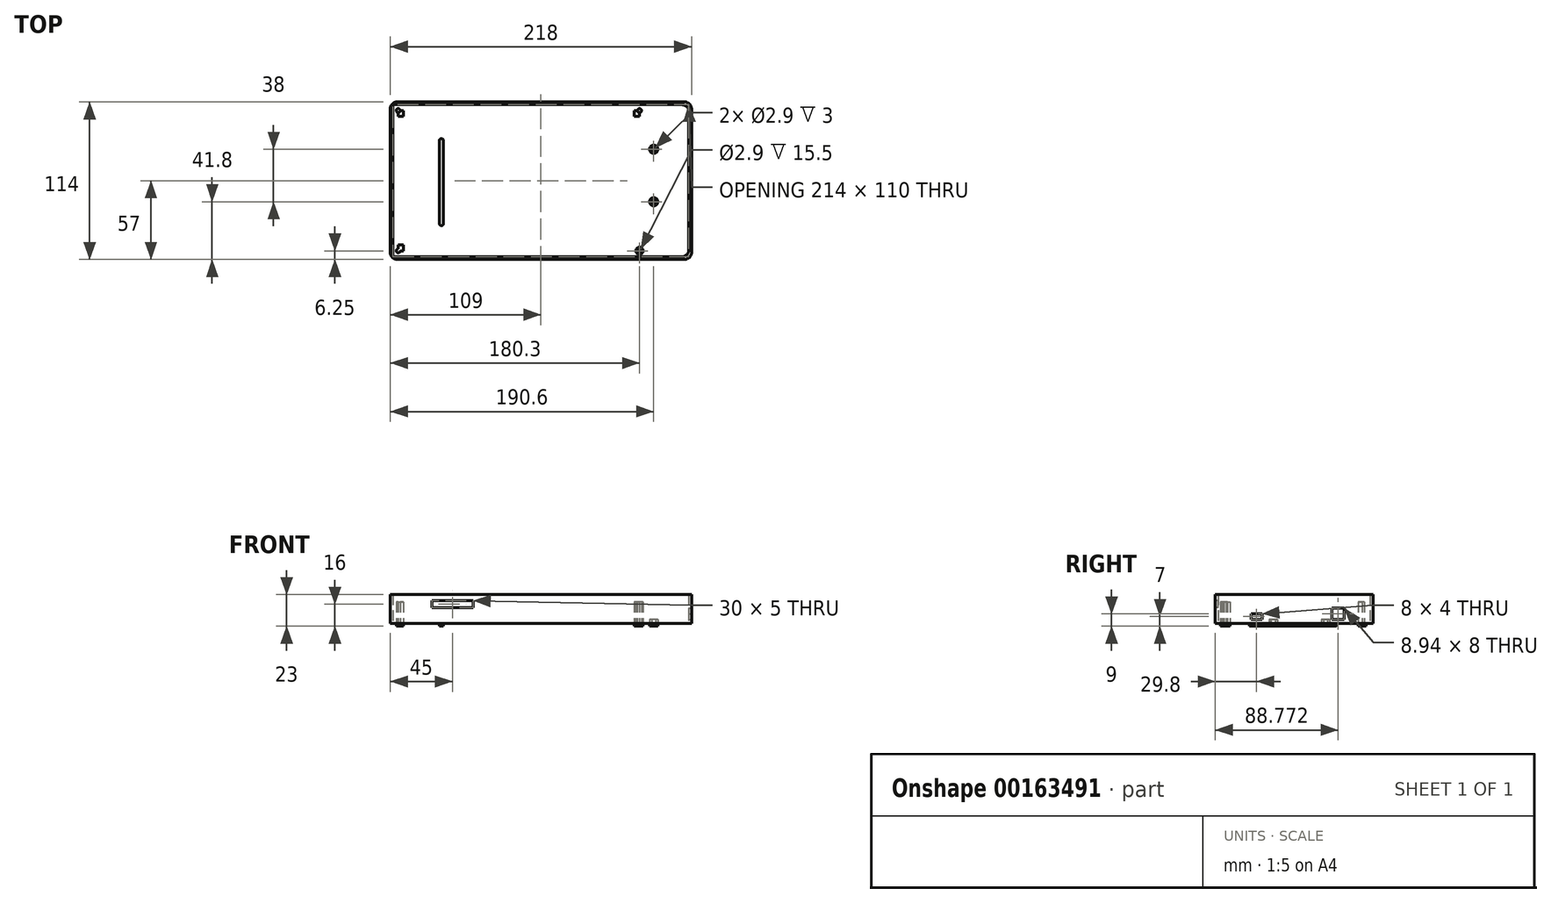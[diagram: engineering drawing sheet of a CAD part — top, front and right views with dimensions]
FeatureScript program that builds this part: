
annotation { "Feature Type Name" : "Feature", "Feature Type Description" : "" }
export const myFeature = defineFeature(function(context is Context, id is Id, definition is map)
    precondition{}
    {
        {
            var Q0;
            Q0=qCreatedBy(makeId("Top.planeOp"),FACE);
            var sketch = newSketch(context, id + "F0", { "sketchPlane" : qUnion([Q0])});
            skLineSegment(sketch, "E0.bottom", {"start": v(87.3, -50.75) * mm, "end": v(-87.3, -50.75) * mm});
            skLineSegment(sketch, "E0.top", {"start": v(87.3, 50.75) * mm, "end": v(-87.3, 50.75) * mm});
            skLineSegment(sketch, "E0.left", {"start": v(87.3, -50.75) * mm, "end": v(87.3, 50.75) * mm});
            skLineSegment(sketch, "E0.right", {"start": v(-87.3, -50.75) * mm, "end": v(-87.3, 50.75) * mm});
            skPoint(sketch, "E0.middle", {"position": v(0, 0) * mm});
            skLineSegment(sketch, "E1.bottom", {"start": v(87.3, 38.3) * mm, "end": v(121, 38.3) * mm, "construction": true});
            skLineSegment(sketch, "E1.top", {"start": v(87.3, -31.2) * mm, "end": v(121, -31.2) * mm, "construction": true});
            skLineSegment(sketch, "E1.left", {"start": v(87.3, 38.3) * mm, "end": v(87.3, -31.2) * mm, "construction": true});
            skLineSegment(sketch, "E1.right", {"start": v(121, 38.3) * mm, "end": v(121, -31.2) * mm, "construction": true});
            skLineSegment(sketch, "E2.bottom", {"start": v(91, -55) * mm, "end": v(-91, -55) * mm});
            skLineSegment(sketch, "E2.top", {"start": v(91, 55) * mm, "end": v(-91, 55) * mm});
            skLineSegment(sketch, "E2.left", {"start": v(91, -55) * mm, "end": v(91, 55) * mm, "construction": true});
            skLineSegment(sketch, "E2.right", {"start": v(-91, -55) * mm, "end": v(-91, 55) * mm});
            skLineSegment(sketch, "E3.bottom", {"start": v(101.5, 38.3) * mm, "end": v(121, 38.3) * mm, "construction": true});
            skLineSegment(sketch, "E3.top", {"start": v(101.5, 27.3) * mm, "end": v(121, 27.3) * mm, "construction": true});
            skLineSegment(sketch, "E3.left", {"start": v(101.5, 38.3) * mm, "end": v(101.5, 27.3) * mm, "construction": true});
            skLineSegment(sketch, "E3.right", {"start": v(121, 38.3) * mm, "end": v(121, 27.3) * mm, "construction": true});
            skLineSegment(sketch, "E4.bottom", {"start": v(-63, -55) * mm, "end": v(-33, -55) * mm, "construction": true});
            skLineSegment(sketch, "E4.top", {"start": v(-63, -33) * mm, "end": v(-33, -33) * mm, "construction": true});
            skLineSegment(sketch, "E4.left", {"start": v(-63, -55) * mm, "end": v(-63, -33) * mm, "construction": true});
            skLineSegment(sketch, "E4.right", {"start": v(-33, -55) * mm, "end": v(-33, -33) * mm, "construction": true});
            skLineSegment(sketch, "E5.bottom", {"start": v(121, 22.8) * mm, "end": v(97.6, 22.8) * mm, "construction": true});
            skLineSegment(sketch, "E5.top", {"start": v(121, -15.2) * mm, "end": v(97.6, -15.2) * mm, "construction": true});
            skLineSegment(sketch, "E5.left", {"start": v(121, 22.8) * mm, "end": v(121, -15.2) * mm, "construction": true});
            skLineSegment(sketch, "E5.right", {"start": v(97.6, 22.8) * mm, "end": v(97.6, -15.2) * mm, "construction": true});
            skLineSegment(sketch, "E6.top", {"start": v(121, -8.2) * mm, "end": v(117, -8.2) * mm, "construction": true});
            skLineSegment(sketch, "E6.left", {"start": v(121, -31.2) * mm, "end": v(121, -8.2) * mm, "construction": true});
            skLineSegment(sketch, "E6.right", {"start": v(117, -31.2) * mm, "end": v(117, -8.2) * mm, "construction": true});
            skLineSegment(sketch, "E7.bottom", {"start": v(121, -31.2) * mm, "end": v(101, -31.2) * mm, "construction": true});
            skLineSegment(sketch, "E7.top", {"start": v(121, -27.2) * mm, "end": v(101, -27.2) * mm, "construction": true});
            skLineSegment(sketch, "E7.left", {"start": v(121, -31.2) * mm, "end": v(121, -27.2) * mm, "construction": true});
            skLineSegment(sketch, "E7.right", {"start": v(101, -31.2) * mm, "end": v(101, -27.2) * mm, "construction": true});
            skLineSegment(sketch, "E8.bottom", {"start": v(-93, 57) * mm, "end": v(125, 57) * mm});
            skLineSegment(sketch, "E8.top", {"start": v(-93, -57) * mm, "end": v(125, -57) * mm});
            skLineSegment(sketch, "E8.left", {"start": v(-93, 57) * mm, "end": v(-93, -57) * mm});
            skLineSegment(sketch, "E8.right", {"start": v(125, 57) * mm, "end": v(125, -57) * mm});
            skCircle(sketch, "E9", {"center": v(-87.3, 50.75) * mm, "radius": 1.45 * mm});
            skCircle(sketch, "E10", {"center": v(-87.3, -50.75) * mm, "radius": 1.45 * mm});
            skCircle(sketch, "E11", {"center": v(87.3, 50.75) * mm, "radius": 1.45 * mm});
            skCircle(sketch, "E12", {"center": v(97.6, 22.8) * mm, "radius": 1.45 * mm});
            skCircle(sketch, "E13", {"center": v(97.6, -15.2) * mm, "radius": 1.45 * mm});
            skCircle(sketch, "E14", {"center": v(117, -8.2) * mm, "radius": 1.75 * mm});
            skCircle(sketch, "E15", {"center": v(101, -27.2) * mm, "radius": 1.75 * mm});
            skCircle(sketch, "E16", {"center": v(97.6, 22.8) * mm, "radius": 3 * mm});
            skCircle(sketch, "E17", {"center": v(97.6, -15.2) * mm, "radius": 3 * mm});
            skLineSegment(sketch, "E18", {"start": v(91, 55) * mm, "end": v(123, 55) * mm});
            skLineSegment(sketch, "E19", {"start": v(123, 55) * mm, "end": v(123, -55) * mm});
            skLineSegment(sketch, "E20", {"start": v(123, -55) * mm, "end": v(91, -55) * mm});
            skLineSegment(sketch, "E21.bottom", {"start": v(-91, 55) * mm, "end": v(-83.6, 55) * mm});
            skLineSegment(sketch, "E21.top", {"start": v(-91, 46.5) * mm, "end": v(-83.6, 46.5) * mm});
            skLineSegment(sketch, "E21.left", {"start": v(-91, 55) * mm, "end": v(-91, 46.5) * mm});
            skLineSegment(sketch, "E21.right", {"start": v(-83.6, 55) * mm, "end": v(-83.6, 46.5) * mm});
            skLineSegment(sketch, "E22.bottom", {"start": v(91, 55) * mm, "end": v(83.6, 55) * mm});
            skLineSegment(sketch, "E22.top", {"start": v(91, 46.5) * mm, "end": v(83.6, 46.5) * mm});
            skLineSegment(sketch, "E22.left", {"start": v(91, 55) * mm, "end": v(91, 46.5) * mm});
            skLineSegment(sketch, "E22.right", {"start": v(83.6, 55) * mm, "end": v(83.6, 46.5) * mm});
            skLineSegment(sketch, "E23.bottom", {"start": v(-91, -55) * mm, "end": v(-83.6, -55) * mm});
            skLineSegment(sketch, "E23.top", {"start": v(-91, -46.5) * mm, "end": v(-83.6, -46.5) * mm});
            skLineSegment(sketch, "E23.left", {"start": v(-91, -55) * mm, "end": v(-91, -46.5) * mm});
            skLineSegment(sketch, "E23.right", {"start": v(-83.6, -55) * mm, "end": v(-83.6, -46.5) * mm});
            skCircle(sketch, "E24", {"center": v(87.3, -50.75) * mm, "radius": 1.45 * mm});
            skCircle(sketch, "E25", {"center": v(87.3, -50.75) * mm, "radius": 2.62 * mm});
            skLineSegment(sketch, "E26.bottom", {"start": v(84.68, -50.75) * mm, "end": v(89.98, -50.75) * mm});
            skLineSegment(sketch, "E26.top", {"start": v(84.68, -55) * mm, "end": v(89.98, -55) * mm});
            skLineSegment(sketch, "E26.left", {"start": v(84.68, -50.75) * mm, "end": v(84.68, -55) * mm});
            skLineSegment(sketch, "E26.right", {"start": v(89.98, -50.75) * mm, "end": v(89.98, -55) * mm});
            skSolve(sketch);
        }
        {
            var Q0;
            {var subQ1=sQuery(id+"F0.wireOp",EDGE,"E0.bottom");var subQ5=sQuery(id+"F0.wireOp",EDGE,"E23.right");var subQ6=makeQuery(id+"F0.imprint","INTERSECT",VERTEX,{"derivedFrom":[subQ1,subQ5]});Q0=makeQuery(id+"F0.imprint","IMPRINT",FACE,{"disambiguationData":[TD([[makeQuery(id+"F0.imprint","IMPRINT",EDGE,{"disambiguationData":[TD([[subQ6,-1.0]])],"derivedFrom":subQ1}),-1.0]])]});}
            var Q1;
            {var subQ0=sQuery(id+"F0.wireOp",EDGE,"E0.right");var subQ1=sQuery(id+"F0.wireOp",EDGE,"E0.bottom");var subQ2=makeQuery(id+"F0.imprint","INTERSECT",VERTEX,{"derivedFrom":[subQ1,subQ0]});Q1=makeQuery(id+"F0.imprint","IMPRINT",FACE,{"disambiguationData":[TD([[makeQuery(id+"F0.imprint","IMPRINT",EDGE,{"disambiguationData":[TD([[subQ2,1.0]])],"derivedFrom":subQ1}),1.0]])]});}
            var Q2;
            Q2=makeQuery(id+"F0.imprint","IMPRINT",FACE,{"disambiguationData":[TD([[makeQuery(id+"F0.imprint","IMPRINT",EDGE,{"derivedFrom":sQuery(id+"F0.wireOp",EDGE,"E2.top")}),-1.0]])]});
            var Q3;
            {var subQ5=sQuery(id+"F0.wireOp",EDGE,"E2.right");Q3=makeQuery(id+"F0.imprint","IMPRINT",FACE,{"disambiguationData":[TD([[makeQuery(id+"F0.imprint","IMPRINT",EDGE,{"derivedFrom":subQ5}),-1.0]])]});}
            var Q4;
            {var subQ8=sQuery(id+"F0.wireOp",EDGE,"E23.bottom");Q4=makeQuery(id+"F0.imprint","IMPRINT",FACE,{"disambiguationData":[TD([[makeQuery(id+"F0.imprint","IMPRINT",EDGE,{"derivedFrom":subQ8}),1.0]])]});}
            var Q5;
            {var subQ0=sQuery(id+"F0.wireOp",EDGE,"E22.bottom");Q5=makeQuery(id+"F0.imprint","IMPRINT",FACE,{"disambiguationData":[TD([[makeQuery(id+"F0.imprint","IMPRINT",EDGE,{"derivedFrom":subQ0}),1.0]])]});}
            var Q6;
            {var subQ0=sQuery(id+"F0.wireOp",EDGE,"E22.right");var subQ3=sQuery(id+"F0.wireOp",EDGE,"E0.top");var subQ4=makeQuery(id+"F0.imprint","INTERSECT",VERTEX,{"derivedFrom":[subQ3,subQ0]});Q6=makeQuery(id+"F0.imprint","IMPRINT",FACE,{"disambiguationData":[TD([[makeQuery(id+"F0.imprint","IMPRINT",EDGE,{"disambiguationData":[TD([[subQ4,-1.0]])],"derivedFrom":subQ3}),1.0]])]});}
            var Q7;
            Q7=makeQuery(id+"F0.imprint","IMPRINT",FACE,{"disambiguationData":[TD([[makeQuery(id+"F0.imprint","IMPRINT",EDGE,{"derivedFrom":sQuery(id+"F0.wireOp",EDGE,"E13")}),-1.0]])]});
            var Q8;
            {var subQ0=sQuery(id+"F0.wireOp",EDGE,"E26.left");Q8=makeQuery(id+"F0.imprint","IMPRINT",FACE,{"disambiguationData":[TD([[makeQuery(id+"F0.imprint","IMPRINT",EDGE,{"derivedFrom":subQ0}),-1.0]])]});}
            var Q9;
            {var subQ0=sQuery(id+"F0.wireOp",EDGE,"E21.right");var subQ7=sQuery(id+"F0.wireOp",EDGE,"E0.top");var subQ9=makeQuery(id+"F0.imprint","INTERSECT",VERTEX,{"derivedFrom":[subQ7,subQ0]});Q9=makeQuery(id+"F0.imprint","IMPRINT",FACE,{"disambiguationData":[TD([[makeQuery(id+"F0.imprint","IMPRINT",EDGE,{"disambiguationData":[TD([[subQ9,-1.0]])],"derivedFrom":subQ7}),1.0]])]});}
            var Q10;
            {var subQ5=sQuery(id+"F0.wireOp",EDGE,"E2.top");Q10=makeQuery(id+"F0.imprint","IMPRINT",FACE,{"disambiguationData":[TD([[makeQuery(id+"F0.imprint","IMPRINT",EDGE,{"derivedFrom":subQ5}),1.0]])]});}
            var Q11;
            {var subQ0=sQuery(id+"F0.wireOp",EDGE,"E11");var subQ1=sQuery(id+"F0.wireOp",EDGE,"E0.top");var subQ2=makeQuery(id+"F0.imprint","INTERSECT",VERTEX,{"derivedFrom":[subQ1,subQ0]});Q11=makeQuery(id+"F0.imprint","IMPRINT",FACE,{"disambiguationData":[TD([[makeQuery(id+"F0.imprint","IMPRINT",EDGE,{"disambiguationData":[TD([[subQ2,-1.0]])],"derivedFrom":subQ1}),1.0]])]});}
            var Q12;
            Q12=makeQuery(id+"F0.imprint","IMPRINT",FACE,{"disambiguationData":[TD([[makeQuery(id+"F0.imprint","IMPRINT",EDGE,{"derivedFrom":sQuery(id+"F0.wireOp",EDGE,"E12")}),-1.0]])]});
            var Q13;
            {var subQ0=sQuery(id+"F0.wireOp",EDGE,"E21.bottom");Q13=makeQuery(id+"F0.imprint","IMPRINT",FACE,{"disambiguationData":[TD([[makeQuery(id+"F0.imprint","IMPRINT",EDGE,{"derivedFrom":subQ0}),-1.0]])]});}
            var Q14;
            {var subQ0=sQuery(id+"F0.wireOp",EDGE,"E0.right");var subQ1=sQuery(id+"F0.wireOp",EDGE,"E0.bottom");var subQ2=makeQuery(id+"F0.imprint","INTERSECT",VERTEX,{"derivedFrom":[subQ1,subQ0]});Q14=makeQuery(id+"F0.imprint","IMPRINT",FACE,{"disambiguationData":[TD([[makeQuery(id+"F0.imprint","IMPRINT",EDGE,{"disambiguationData":[TD([[subQ2,1.0]])],"derivedFrom":subQ1}),-1.0]])]});}
            var Q15;
            Q15=makeQuery(id+"F0.imprint","IMPRINT",FACE,{"disambiguationData":[TD([[makeQuery(id+"F0.imprint","IMPRINT",EDGE,{"derivedFrom":sQuery(id+"F0.wireOp",EDGE,"E13")}),1.0]])]});
            var Q16;
            Q16=makeQuery(id+"F0.imprint","IMPRINT",FACE,{"disambiguationData":[TD([[makeQuery(id+"F0.imprint","IMPRINT",EDGE,{"derivedFrom":sQuery(id+"F0.wireOp",EDGE,"E14")}),1.0]])]});
            var Q17;
            Q17=makeQuery(id+"F0.imprint","IMPRINT",FACE,{"disambiguationData":[TD([[makeQuery(id+"F0.imprint","IMPRINT",EDGE,{"derivedFrom":sQuery(id+"F0.wireOp",EDGE,"E12")}),1.0]])]});
            var Q18;
            Q18=makeQuery(id+"F0.imprint","IMPRINT",FACE,{"disambiguationData":[TD([[makeQuery(id+"F0.imprint","IMPRINT",EDGE,{"derivedFrom":sQuery(id+"F0.wireOp",EDGE,"E15")}),1.0]])]});
            var Q19;
            {var subQ0=sQuery(id+"F0.wireOp",EDGE,"E0.left");var subQ1=sQuery(id+"F0.wireOp",EDGE,"E0.top");var subQ2=makeQuery(id+"F0.imprint","INTERSECT",VERTEX,{"derivedFrom":[subQ1,subQ0]});Q19=makeQuery(id+"F0.imprint","IMPRINT",FACE,{"disambiguationData":[TD([[makeQuery(id+"F0.imprint","IMPRINT",EDGE,{"disambiguationData":[TD([[subQ2,-1.0]])],"derivedFrom":subQ1}),-1.0]])]});}
            var Q20;
            {var subQ0=sQuery(id+"F0.wireOp",EDGE,"E0.right");var subQ1=sQuery(id+"F0.wireOp",EDGE,"E0.top");var subQ2=makeQuery(id+"F0.imprint","INTERSECT",VERTEX,{"derivedFrom":[subQ1,subQ0]});Q20=makeQuery(id+"F0.imprint","IMPRINT",FACE,{"disambiguationData":[TD([[makeQuery(id+"F0.imprint","IMPRINT",EDGE,{"disambiguationData":[TD([[subQ2,1.0]])],"derivedFrom":subQ1}),1.0]])]});}
            var Q21;
            {var subQ0=sQuery(id+"F0.wireOp",EDGE,"E0.left");var subQ1=sQuery(id+"F0.wireOp",EDGE,"E0.top");var subQ2=makeQuery(id+"F0.imprint","INTERSECT",VERTEX,{"derivedFrom":[subQ1,subQ0]});Q21=makeQuery(id+"F0.imprint","IMPRINT",FACE,{"disambiguationData":[TD([[makeQuery(id+"F0.imprint","IMPRINT",EDGE,{"disambiguationData":[TD([[subQ2,-1.0]])],"derivedFrom":subQ1}),1.0]])]});}
            var Q22;
            {var subQ0=sQuery(id+"F0.wireOp",EDGE,"E0.right");var subQ1=sQuery(id+"F0.wireOp",EDGE,"E0.top");var subQ2=makeQuery(id+"F0.imprint","INTERSECT",VERTEX,{"derivedFrom":[subQ1,subQ0]});Q22=makeQuery(id+"F0.imprint","IMPRINT",FACE,{"disambiguationData":[TD([[makeQuery(id+"F0.imprint","IMPRINT",EDGE,{"disambiguationData":[TD([[subQ2,1.0]])],"derivedFrom":subQ1}),-1.0]])]});}
            var Q23;
            Q23=makeQuery(id+"F0.imprint","IMPRINT",FACE,{"disambiguationData":[TD([[makeQuery(id+"F0.imprint","IMPRINT",EDGE,{"derivedFrom":sQuery(id+"F0.wireOp",EDGE,"E14")}),-1.0]])]});
            var Q24;
            {var subQ0=sQuery(id+"F0.wireOp",EDGE,"E26.bottom");var subQ1=sQuery(id+"F0.wireOp",EDGE,"E24");var subQ2=makeQuery(id+"F0.imprint","INTERSECT",VERTEX,{"disambiguationData":[OD(0.0)],"derivedFrom":[subQ1,subQ0]});Q24=makeQuery(id+"F0.imprint","IMPRINT",FACE,{"disambiguationData":[TD([[makeQuery(id+"F0.imprint","IMPRINT",EDGE,{"disambiguationData":[TD([[subQ2,1.0]])],"derivedFrom":subQ1}),1.0]])]});}
            var Q25;
            {var subQ0=sQuery(id+"F0.wireOp",EDGE,"E26.bottom");var subQ1=sQuery(id+"F0.wireOp",EDGE,"E0.left");var subQ2=makeQuery(id+"F0.imprint","INTERSECT",VERTEX,{"derivedFrom":[subQ1,subQ0]});Q25=makeQuery(id+"F0.imprint","IMPRINT",FACE,{"disambiguationData":[TD([[makeQuery(id+"F0.imprint","IMPRINT",EDGE,{"disambiguationData":[TD([[subQ2,-1.0]])],"derivedFrom":subQ1}),1.0]])]});}
            var Q26;
            {var subQ0=sQuery(id+"F0.wireOp",EDGE,"E26.bottom");var subQ1=sQuery(id+"F0.wireOp",EDGE,"E0.left");var subQ2=makeQuery(id+"F0.imprint","INTERSECT",VERTEX,{"derivedFrom":[subQ1,subQ0]});Q26=makeQuery(id+"F0.imprint","IMPRINT",FACE,{"disambiguationData":[TD([[makeQuery(id+"F0.imprint","IMPRINT",EDGE,{"disambiguationData":[TD([[subQ2,-1.0]])],"derivedFrom":subQ1}),-1.0]])]});}
            var Q27;
            {var subQ0=sQuery(id+"F0.wireOp",EDGE,"E24");var subQ1=sQuery(id+"F0.wireOp",EDGE,"E0.left");var subQ2=makeQuery(id+"F0.imprint","INTERSECT",VERTEX,{"derivedFrom":[subQ1,subQ0]});Q27=makeQuery(id+"F0.imprint","IMPRINT",FACE,{"disambiguationData":[TD([[makeQuery(id+"F0.imprint","IMPRINT",EDGE,{"disambiguationData":[TD([[subQ2,-1.0]])],"derivedFrom":subQ1}),1.0]])]});}
            var Q28;
            {var subQ0=sQuery(id+"F0.wireOp",EDGE,"E24");var subQ1=sQuery(id+"F0.wireOp",EDGE,"E0.left");var subQ2=makeQuery(id+"F0.imprint","INTERSECT",VERTEX,{"derivedFrom":[subQ1,subQ0]});Q28=makeQuery(id+"F0.imprint","IMPRINT",FACE,{"disambiguationData":[TD([[makeQuery(id+"F0.imprint","IMPRINT",EDGE,{"disambiguationData":[TD([[subQ2,-1.0]])],"derivedFrom":subQ1}),-1.0]])]});}
            var Q29;
            Q29=makeQuery(id+"F0.imprint","IMPRINT",FACE,{"disambiguationData":[TD([[makeQuery(id+"F0.imprint","IMPRINT",EDGE,{"derivedFrom":sQuery(id+"F0.wireOp",EDGE,"E26.top")}),1.0]])]});
            var Q30;
            {var subQ0=sQuery(id+"F0.wireOp",EDGE,"E26.bottom");var subQ1=sQuery(id+"F0.wireOp",EDGE,"E24");var subQ2=makeQuery(id+"F0.imprint","INTERSECT",VERTEX,{"disambiguationData":[OD(0.0)],"derivedFrom":[subQ1,subQ0]});Q30=makeQuery(id+"F0.imprint","IMPRINT",FACE,{"disambiguationData":[TD([[makeQuery(id+"F0.imprint","IMPRINT",EDGE,{"disambiguationData":[TD([[subQ2,1.0]])],"derivedFrom":subQ1}),-1.0]])]});}
            extrude(context, id + "F1", {"entities" : qUnion([Q0, Q1, Q2, Q3, Q4, Q5, Q6, Q7, Q8, Q9, Q10, Q11, Q12, Q13, Q14, Q15, Q16, Q17, Q18, Q19, Q20, Q21, Q22, Q23, Q24, Q25, Q26, Q27, Q28, Q29, Q30]), "depth" : 2 * mm});
        }
        {
            var Q0;
            Q0=makeQuery(id+"F0.imprint","IMPRINT",FACE,{"disambiguationData":[TD([[makeQuery(id+"F0.imprint","IMPRINT",EDGE,{"derivedFrom":sQuery(id+"F0.wireOp",EDGE,"E12")}),-1.0]])]});
            var Q1;
            Q1=makeQuery(id+"F0.imprint","IMPRINT",FACE,{"disambiguationData":[TD([[makeQuery(id+"F0.imprint","IMPRINT",EDGE,{"derivedFrom":sQuery(id+"F0.wireOp",EDGE,"E13")}),-1.0]])]});
            extrude(context, id + "F2", {"entities" : qUnion([Q0, Q1]), "operationType" : NewBodyOperationType.ADD, "depth" : 5 * mm});
        }
        {
            var Q0;
            {var subQ4=sQuery(id+"F0.wireOp",EDGE,"E2.bottom");Q0=makeQuery(id+"F0.imprint","IMPRINT",FACE,{"disambiguationData":[TD([[makeQuery(id+"F0.imprint","IMPRINT",EDGE,{"derivedFrom":subQ4}),1.0]])]});}
            extrude(context, id + "F3", {"entities" : qUnion([Q0]), "depth" : 23 * mm});
        }
        {
            var Q0;
            {var subQ0=sQuery(id+"F0.wireOp",EDGE,"E21.right");var subQ7=sQuery(id+"F0.wireOp",EDGE,"E0.top");var subQ9=makeQuery(id+"F0.imprint","INTERSECT",VERTEX,{"derivedFrom":[subQ7,subQ0]});Q0=makeQuery(id+"F0.imprint","IMPRINT",FACE,{"disambiguationData":[TD([[makeQuery(id+"F0.imprint","IMPRINT",EDGE,{"disambiguationData":[TD([[subQ9,-1.0]])],"derivedFrom":subQ7}),1.0]])]});}
            var Q1;
            {var subQ0=sQuery(id+"F0.wireOp",EDGE,"E21.bottom");Q1=makeQuery(id+"F0.imprint","IMPRINT",FACE,{"disambiguationData":[TD([[makeQuery(id+"F0.imprint","IMPRINT",EDGE,{"derivedFrom":subQ0}),-1.0]])]});}
            var Q2;
            {var subQ8=sQuery(id+"F0.wireOp",EDGE,"E23.bottom");Q2=makeQuery(id+"F0.imprint","IMPRINT",FACE,{"disambiguationData":[TD([[makeQuery(id+"F0.imprint","IMPRINT",EDGE,{"derivedFrom":subQ8}),1.0]])]});}
            var Q3;
            {var subQ1=sQuery(id+"F0.wireOp",EDGE,"E0.bottom");var subQ5=sQuery(id+"F0.wireOp",EDGE,"E23.right");var subQ6=makeQuery(id+"F0.imprint","INTERSECT",VERTEX,{"derivedFrom":[subQ1,subQ5]});Q3=makeQuery(id+"F0.imprint","IMPRINT",FACE,{"disambiguationData":[TD([[makeQuery(id+"F0.imprint","IMPRINT",EDGE,{"disambiguationData":[TD([[subQ6,-1.0]])],"derivedFrom":subQ1}),-1.0]])]});}
            var Q4;
            {var subQ0=sQuery(id+"F0.wireOp",EDGE,"E0.right");var subQ1=sQuery(id+"F0.wireOp",EDGE,"E0.bottom");var subQ2=makeQuery(id+"F0.imprint","INTERSECT",VERTEX,{"derivedFrom":[subQ1,subQ0]});Q4=makeQuery(id+"F0.imprint","IMPRINT",FACE,{"disambiguationData":[TD([[makeQuery(id+"F0.imprint","IMPRINT",EDGE,{"disambiguationData":[TD([[subQ2,1.0]])],"derivedFrom":subQ1}),1.0]])]});}
            var Q5;
            {var subQ0=sQuery(id+"F0.wireOp",EDGE,"E0.right");var subQ1=sQuery(id+"F0.wireOp",EDGE,"E0.bottom");var subQ2=makeQuery(id+"F0.imprint","INTERSECT",VERTEX,{"derivedFrom":[subQ1,subQ0]});Q5=makeQuery(id+"F0.imprint","IMPRINT",FACE,{"disambiguationData":[TD([[makeQuery(id+"F0.imprint","IMPRINT",EDGE,{"disambiguationData":[TD([[subQ2,1.0]])],"derivedFrom":subQ1}),-1.0]])]});}
            var Q6;
            {var subQ0=sQuery(id+"F0.wireOp",EDGE,"E22.bottom");Q6=makeQuery(id+"F0.imprint","IMPRINT",FACE,{"disambiguationData":[TD([[makeQuery(id+"F0.imprint","IMPRINT",EDGE,{"derivedFrom":subQ0}),1.0]])]});}
            var Q7;
            {var subQ0=sQuery(id+"F0.wireOp",EDGE,"E11");var subQ1=sQuery(id+"F0.wireOp",EDGE,"E0.top");var subQ2=makeQuery(id+"F0.imprint","INTERSECT",VERTEX,{"derivedFrom":[subQ1,subQ0]});Q7=makeQuery(id+"F0.imprint","IMPRINT",FACE,{"disambiguationData":[TD([[makeQuery(id+"F0.imprint","IMPRINT",EDGE,{"disambiguationData":[TD([[subQ2,-1.0]])],"derivedFrom":subQ1}),1.0]])]});}
            var Q8;
            {var subQ0=sQuery(id+"F0.wireOp",EDGE,"E24");var subQ1=sQuery(id+"F0.wireOp",EDGE,"E0.left");var subQ2=makeQuery(id+"F0.imprint","INTERSECT",VERTEX,{"derivedFrom":[subQ1,subQ0]});Q8=makeQuery(id+"F0.imprint","IMPRINT",FACE,{"disambiguationData":[TD([[makeQuery(id+"F0.imprint","IMPRINT",EDGE,{"disambiguationData":[TD([[subQ2,-1.0]])],"derivedFrom":subQ1}),1.0]])]});}
            var Q9;
            {var subQ0=sQuery(id+"F0.wireOp",EDGE,"E24");var subQ1=sQuery(id+"F0.wireOp",EDGE,"E0.left");var subQ2=makeQuery(id+"F0.imprint","INTERSECT",VERTEX,{"derivedFrom":[subQ1,subQ0]});Q9=makeQuery(id+"F0.imprint","IMPRINT",FACE,{"disambiguationData":[TD([[makeQuery(id+"F0.imprint","IMPRINT",EDGE,{"disambiguationData":[TD([[subQ2,-1.0]])],"derivedFrom":subQ1}),-1.0]])]});}
            var Q10;
            {var subQ0=sQuery(id+"F0.wireOp",EDGE,"E26.bottom");var subQ1=sQuery(id+"F0.wireOp",EDGE,"E24");var subQ2=makeQuery(id+"F0.imprint","INTERSECT",VERTEX,{"disambiguationData":[OD(0.0)],"derivedFrom":[subQ1,subQ0]});Q10=makeQuery(id+"F0.imprint","IMPRINT",FACE,{"disambiguationData":[TD([[makeQuery(id+"F0.imprint","IMPRINT",EDGE,{"disambiguationData":[TD([[subQ2,1.0]])],"derivedFrom":subQ1}),-1.0]])]});}
            var Q11;
            Q11=makeQuery(id+"F0.imprint","IMPRINT",FACE,{"disambiguationData":[TD([[makeQuery(id+"F0.imprint","IMPRINT",EDGE,{"derivedFrom":sQuery(id+"F0.wireOp",EDGE,"E26.top")}),1.0]])]});
            var Q12;
            Q12=sQuery(id+"F0.wireOp",EDGE,"E9");
            var Q13;
            Q13=sQuery(id+"F0.wireOp",EDGE,"E11");
            var Q14;
            Q14=sQuery(id+"F0.wireOp",EDGE,"fiGOuGzB-O6sn-Jjxz-VzIu-r24W9GTNH7oX");
            var Q15;
            Q15=sQuery(id+"F0.wireOp",EDGE,"E10");
            extrude(context, id + "F4", {"entities" : qUnion([Q0, Q1, Q2, Q3, Q4, Q5, Q6, Q7, Q8, Q9, Q10, Q11]), "operationType" : NewBodyOperationType.ADD, "surfaceEntities" : qUnion([Q12, Q13, Q14, Q15]), "depth" : 17.5 * mm});
        }
        {
            var Q0;
            {var subQ0=sQuery(id+"F0.wireOp",EDGE,"E8.top");Q0=makeQuery(id+"F3.boolean.opBoolean","MERGE",FACE,{"derivedFrom":[makeQuery(id+"F1.opExtrude","SWEPT_FACE",FACE,{"disambiguationData":[OSD([subQ0])]}),makeQuery(id+"F3.opExtrude","SWEPT_FACE",FACE,{"disambiguationData":[OSD([subQ0])]})]});}
            var sketch = newSketch(context, id + "F5", { "sketchPlane" : qUnion([Q0])});
            skPoint(sketch, "E27.0", {"position": v(-63, 0) * mm});
            skPoint(sketch, "E28.0", {"position": v(-33, 0) * mm});
            skLineSegment(sketch, "E29.0", {"start": v(-91, 17.5) * mm, "end": v(-83.6, 17.5) * mm});
            skLineSegment(sketch, "E30.bottom", {"start": v(-63, 0) * mm, "end": v(-33, 0) * mm, "construction": true});
            skLineSegment(sketch, "E30.top", {"start": v(-63, 17.5) * mm, "end": v(-33, 17.5) * mm, "construction": true});
            skLineSegment(sketch, "E30.left", {"start": v(-63, 0) * mm, "end": v(-63, 17.5) * mm, "construction": true});
            skLineSegment(sketch, "E30.right", {"start": v(-33, 0) * mm, "end": v(-33, 17.5) * mm, "construction": true});
            skLineSegment(sketch, "E31.bottom", {"start": v(-63, 17.5) * mm, "end": v(-33, 17.5) * mm});
            skLineSegment(sketch, "E31.top", {"start": v(-63, 13.5) * mm, "end": v(-33, 13.5) * mm});
            skLineSegment(sketch, "E31.left", {"start": v(-63, 17.5) * mm, "end": v(-63, 13.5) * mm});
            skLineSegment(sketch, "E31.right", {"start": v(-33, 17.5) * mm, "end": v(-33, 13.5) * mm});
            skLineSegment(sketch, "E32.top", {"start": v(-63, 18.5) * mm, "end": v(-33, 18.5) * mm});
            skLineSegment(sketch, "E32.left", {"start": v(-63, 17.5) * mm, "end": v(-63, 18.5) * mm});
            skLineSegment(sketch, "E32.right", {"start": v(-33, 17.5) * mm, "end": v(-33, 18.5) * mm});
            skSolve(sketch);
        }
        {
            var Q0;
            Q0=makeQuery(id+"F5.imprint","IMPRINT",FACE,{"disambiguationData":[TD([[makeQuery(id+"F5.imprint","IMPRINT",EDGE,{"derivedFrom":sQuery(id+"F5.wireOp",EDGE,"E31.top")}),1.0]])]});
            var Q1;
            Q1=makeQuery(id+"F5.imprint","IMPRINT",FACE,{"disambiguationData":[TD([[makeQuery(id+"F5.imprint","IMPRINT",EDGE,{"derivedFrom":sQuery(id+"F5.wireOp",EDGE,"E31.bottom")}),1.0]])]});
            var Q2;
            Q2=makeQuery(id+"F3.opExtrude","SWEPT_FACE",FACE,{"disambiguationData":[OSD([sQuery(id+"F0.wireOp",EDGE,"E2.bottom"),sQuery(id+"F0.wireOp",EDGE,"E20"),sQuery(id+"F0.wireOp",EDGE,"E23.bottom")])]});
            extrude(context, id + "F6", {"entities" : qUnion([Q0, Q1]), "operationType" : NewBodyOperationType.REMOVE, "endBound" : BoundingType.UP_TO_SURFACE, "oppositeDirection" : true, "endBoundEntityFace" : qUnion([Q2]), "depth" : 25 * mm});
        }
        {
            var Q0;
            {var subQ0=sQuery(id+"F0.wireOp",EDGE,"E8.right");Q0=makeQuery(id+"F3.boolean.opBoolean","MERGE",FACE,{"derivedFrom":[makeQuery(id+"F1.opExtrude","SWEPT_FACE",FACE,{"disambiguationData":[OSD([subQ0])]}),makeQuery(id+"F3.opExtrude","SWEPT_FACE",FACE,{"disambiguationData":[OSD([subQ0])]})]});}
            var sketch = newSketch(context, id + "F7", { "sketchPlane" : qUnion([Q0])});
            skPoint(sketch, "E33.0", {"position": v(38.3, 0) * mm});
            skPoint(sketch, "E34.0", {"position": v(27.3, 0) * mm});
            skPoint(sketch, "E35.0", {"position": v(-27.2, 0) * mm});
            skPoint(sketch, "E36.0", {"position": v(-31.2, 0) * mm});
            skLineSegment(sketch, "E37.0", {"start": v(-18.2, 5) * mm, "end": v(-12.2, 5) * mm});
            skLineSegment(sketch, "E38.bottom", {"start": v(27.3, 0) * mm, "end": v(36.24, 0) * mm, "construction": true});
            skLineSegment(sketch, "E38.top", {"start": v(27.3, 5) * mm, "end": v(36.24, 5) * mm, "construction": true});
            skLineSegment(sketch, "E38.left", {"start": v(27.3, 0) * mm, "end": v(27.3, 5) * mm, "construction": true});
            skLineSegment(sketch, "E38.right", {"start": v(36.24, 0) * mm, "end": v(36.24, 5) * mm, "construction": true});
            skLineSegment(sketch, "E39.bottom", {"start": v(-31.2, 0) * mm, "end": v(-27.2, 0) * mm, "construction": true});
            skLineSegment(sketch, "E39.left", {"start": v(-31.2, 0) * mm, "end": v(-31.2, 5) * mm, "construction": true});
            skLineSegment(sketch, "E39.right", {"start": v(-27.2, 0) * mm, "end": v(-27.2, 5) * mm, "construction": true});
            skLineSegment(sketch, "E40.bottom", {"start": v(27.3, 5) * mm, "end": v(36.24, 5) * mm});
            skLineSegment(sketch, "E40.top", {"start": v(27.3, 13) * mm, "end": v(36.24, 13) * mm});
            skLineSegment(sketch, "E40.left", {"start": v(27.3, 5) * mm, "end": v(27.3, 13) * mm});
            skLineSegment(sketch, "E40.right", {"start": v(36.24, 5) * mm, "end": v(36.24, 13) * mm});
            skLineSegment(sketch, "E41.0.0", {"start": v(-57, 0) * mm, "end": v(57, 0) * mm});
            skLineSegment(sketch, "E41.0.1", {"start": v(57, 0) * mm, "end": v(57, 2) * mm});
            skLineSegment(sketch, "E41.0.2", {"start": v(58.1, 23) * mm, "end": v(-57, 23) * mm});
            skLineSegment(sketch, "E41.0.3", {"start": v(-57, 23) * mm, "end": v(-57, 0) * mm});
            skPoint(sketch, "E42.right.end.orphan", {"position": v(-27.2, 9) * mm});
            skLineSegment(sketch, "E43.bottom", {"start": v(-31.2, 5) * mm, "end": v(-23.2, 5) * mm});
            skLineSegment(sketch, "E43.top", {"start": v(-31.2, 9) * mm, "end": v(-23.2, 9) * mm});
            skLineSegment(sketch, "E43.left", {"start": v(-31.2, 5) * mm, "end": v(-31.2, 9) * mm});
            skLineSegment(sketch, "E43.right", {"start": v(-23.2, 5) * mm, "end": v(-23.2, 9) * mm});
            skSolve(sketch);
        }
        {
            var Q0;
            Q0=makeQuery(id+"F7.imprint","IMPRINT",FACE,{"disambiguationData":[TD([[makeQuery(id+"F7.imprint","IMPRINT",EDGE,{"derivedFrom":sQuery(id+"F7.wireOp",EDGE,"E43.bottom")}),1.0]])]});
            var Q1;
            Q1=makeQuery(id+"F7.imprint","IMPRINT",FACE,{"disambiguationData":[TD([[makeQuery(id+"F7.imprint","IMPRINT",EDGE,{"derivedFrom":sQuery(id+"F7.wireOp",EDGE,"E40.bottom")}),1.0]])]});
            var Q2;
            Q2=makeQuery(id+"F3.opExtrude","SWEPT_FACE",FACE,{"disambiguationData":[OSD([sQuery(id+"F0.wireOp",EDGE,"E19")])]});
            extrude(context, id + "F8", {"entities" : qUnion([Q0, Q1]), "operationType" : NewBodyOperationType.REMOVE, "endBound" : BoundingType.UP_TO_SURFACE, "oppositeDirection" : true, "endBoundEntityFace" : qUnion([Q2]), "depth" : 25 * mm});
        }
        {
            var Q0;
            {var subQ0=sQuery(id+"F0.wireOp",EDGE,"E8.left");var subQ1=sQuery(id+"F0.wireOp",EDGE,"E8.top");Q0=makeQuery(id+"F3.boolean.opBoolean","MERGE",EDGE,{"derivedFrom":[makeQuery(id+"F1.opExtrude","SWEPT_EDGE",EDGE,{"disambiguationData":[OSD([subQ1,subQ0])]}),makeQuery(id+"F3.opExtrude","SWEPT_EDGE",EDGE,{"disambiguationData":[OSD([subQ1,subQ0])]})]});}
            var Q1;
            {var subQ0=sQuery(id+"F0.wireOp",EDGE,"E8.left");var subQ1=sQuery(id+"F0.wireOp",EDGE,"E8.bottom");Q1=makeQuery(id+"F3.boolean.opBoolean","MERGE",EDGE,{"derivedFrom":[makeQuery(id+"F1.opExtrude","SWEPT_EDGE",EDGE,{"disambiguationData":[OSD([subQ1,subQ0])]}),makeQuery(id+"F3.opExtrude","SWEPT_EDGE",EDGE,{"disambiguationData":[OSD([subQ1,subQ0])]})]});}
            var Q2;
            {var subQ0=sQuery(id+"F0.wireOp",EDGE,"E8.right");var subQ1=sQuery(id+"F0.wireOp",EDGE,"E8.bottom");Q2=makeQuery(id+"F3.boolean.opBoolean","MERGE",EDGE,{"derivedFrom":[makeQuery(id+"F1.opExtrude","SWEPT_EDGE",EDGE,{"disambiguationData":[OSD([subQ1,subQ0])]}),makeQuery(id+"F3.opExtrude","SWEPT_EDGE",EDGE,{"disambiguationData":[OSD([subQ1,subQ0])]})]});}
            var Q3;
            {var subQ0=sQuery(id+"F0.wireOp",EDGE,"E8.right");var subQ1=sQuery(id+"F0.wireOp",EDGE,"E8.top");Q3=makeQuery(id+"F3.boolean.opBoolean","MERGE",EDGE,{"derivedFrom":[makeQuery(id+"F1.opExtrude","SWEPT_EDGE",EDGE,{"disambiguationData":[OSD([subQ1,subQ0])]}),makeQuery(id+"F3.opExtrude","SWEPT_EDGE",EDGE,{"disambiguationData":[OSD([subQ1,subQ0])]})]});}
            fillet(context, id + "F9", {"entities" : qUnion([Q0, Q1, Q2, Q3]), "radius" : 5 * mm, "tangentPropagation" : true, "allowEdgeOverflow" : false});
        }
        {
            var Q0;
            Q0=makeQuery(id+"F3.opExtrude","SWEPT_EDGE",EDGE,{"disambiguationData":[OSD([sQuery(id+"F0.wireOp",EDGE,"E21.bottom"),sQuery(id+"F0.wireOp",EDGE,"E21.left")])]});
            var Q1;
            Q1=makeQuery(id+"F3.opExtrude","SWEPT_EDGE",EDGE,{"disambiguationData":[OSD([sQuery(id+"F0.wireOp",EDGE,"E18"),sQuery(id+"F0.wireOp",EDGE,"E19")])]});
            var Q2;
            Q2=makeQuery(id+"F3.opExtrude","SWEPT_EDGE",EDGE,{"disambiguationData":[OSD([sQuery(id+"F0.wireOp",EDGE,"E19"),sQuery(id+"F0.wireOp",EDGE,"E20")])]});
            var Q3;
            Q3=makeQuery(id+"F3.opExtrude","SWEPT_EDGE",EDGE,{"disambiguationData":[OSD([sQuery(id+"F0.wireOp",EDGE,"E23.bottom"),sQuery(id+"F0.wireOp",EDGE,"E23.left")])]});
            fillet(context, id + "F10", {"entities" : qUnion([Q0, Q1, Q2, Q3]), "radius" : 5 * mm, "tangentPropagation" : true, "allowEdgeOverflow" : false});
        }
        {
            var Q0;
            {var subQ1=sQuery(id+"F0.wireOp",EDGE,"E8.left");var subQ4=sQuery(id+"F0.wireOp",EDGE,"E8.bottom");var subQ5=makeQuery(id+"F1.opExtrude","SWEPT_FACE",FACE,{"disambiguationData":[OSD([subQ4])]});var subQ6=sQuery(id+"F0.wireOp",EDGE,"E8.top");var subQ8=sQuery(id+"F0.wireOp",EDGE,"E8.right");Q0=makeQuery(id+"F4.boolean.opBoolean","SPLIT",FACE,{"disambiguationData":[TD([subQ5])],"derivedFrom":makeQuery(id+"F2.boolean.opBoolean","SPLIT",FACE,{"disambiguationData":[TD([subQ5])],"derivedFrom":makeQuery(id+"F1.opExtrude","CAP_FACE",FACE,{"disambiguationData":[OSD([subQ4,subQ6,subQ1,subQ8])],"isStart":false})})});}
            var sketch = newSketch(context, id + "F11", { "sketchPlane" : qUnion([Q0])});
            skLineSegment(sketch, "E44.0.0", {"start": v(123, -50) * mm, "end": v(123, 50) * mm, "construction": true});
            skArc(sketch, "E44.0.1", {"start": v(123, 50) * mm, "mid": v(121.54, 53.54) * mm, "end": v(118, 55) * mm, "construction": true});
            skLineSegment(sketch, "E44.0.2", {"start": v(118, 55) * mm, "end": v(91, 55) * mm, "construction": true});
            skLineSegment(sketch, "E44.0.3", {"start": v(91, 55) * mm, "end": v(91, 46.5) * mm, "construction": true});
            skLineSegment(sketch, "E44.0.4", {"start": v(91, 46.5) * mm, "end": v(83.6, 46.5) * mm, "construction": true});
            skLineSegment(sketch, "E44.0.5", {"start": v(83.6, 46.5) * mm, "end": v(83.6, 55) * mm, "construction": true});
            skLineSegment(sketch, "E44.0.6", {"start": v(83.6, 55) * mm, "end": v(-83.6, 55) * mm, "construction": true});
            skLineSegment(sketch, "E44.0.7", {"start": v(-83.6, 55) * mm, "end": v(-83.6, 46.5) * mm, "construction": true});
            skLineSegment(sketch, "E44.0.8", {"start": v(-83.6, 46.5) * mm, "end": v(-91, 46.5) * mm, "construction": true});
            skLineSegment(sketch, "E44.0.9", {"start": v(-91, 46.5) * mm, "end": v(-91, -46.5) * mm, "construction": true});
            skLineSegment(sketch, "E44.0.10", {"start": v(-91, -46.5) * mm, "end": v(-83.6, -46.5) * mm, "construction": true});
            skLineSegment(sketch, "E44.0.11", {"start": v(-83.6, -46.5) * mm, "end": v(-83.6, -55) * mm, "construction": true});
            skLineSegment(sketch, "E44.0.12", {"start": v(-83.6, -55) * mm, "end": v(118, -55) * mm, "construction": true});
            skArc(sketch, "E44.0.13", {"start": v(118, -55) * mm, "mid": v(121.54, -53.54) * mm, "end": v(123, -50) * mm, "construction": true});
            skLineSegment(sketch, "E45.bottom", {"start": v(-61, 29) * mm, "end": v(59, 29) * mm, "construction": true});
            skLineSegment(sketch, "E45.top", {"start": v(-61, -31) * mm, "end": v(59, -31) * mm, "construction": true});
            skLineSegment(sketch, "E45.left", {"start": v(-61, 29) * mm, "end": v(-61, -31) * mm, "construction": true});
            skLineSegment(sketch, "E45.right", {"start": v(59, 29) * mm, "end": v(59, -31) * mm, "construction": true});
            skLineSegment(sketch, "E46", {"start": v(-56, 29) * mm, "end": v(-56, -31) * mm, "construction": true});
            skArc(sketch, "E47.0.startCap", {"start": v(-57.5, 29) * mm, "mid": v(-56, 30.5) * mm, "end": v(-54.5, 29) * mm});
            skArc(sketch, "E47.0.endCap", {"start": v(-54.5, -31) * mm, "mid": v(-56, -32.5) * mm, "end": v(-57.5, -31) * mm});
            skLineSegment(sketch, "E47.0.left", {"start": v(-54.5, 29) * mm, "end": v(-54.5, -31) * mm});
            skLineSegment(sketch, "E47.0.right", {"start": v(-57.5, 29) * mm, "end": v(-57.5, -31) * mm});
            skLineSegment(sketch, "E48.1.0.0", {"start": v(-44.5, 29) * mm, "end": v(-44.5, -31) * mm});
            skLineSegment(sketch, "E48.1.0.1", {"start": v(-47.5, 29) * mm, "end": v(-47.5, -31) * mm});
            skArc(sketch, "E48.1.0.2", {"start": v(-47.5, 29) * mm, "mid": v(-46, 30.5) * mm, "end": v(-44.5, 29) * mm});
            skArc(sketch, "E48.1.0.3", {"start": v(-44.5, -31) * mm, "mid": v(-46, -32.5) * mm, "end": v(-47.5, -31) * mm});
            skLineSegment(sketch, "E48.2.0.0", {"start": v(-34.5, 29) * mm, "end": v(-34.5, -31) * mm});
            skLineSegment(sketch, "E48.2.0.1", {"start": v(-37.5, 29) * mm, "end": v(-37.5, -31) * mm});
            skArc(sketch, "E48.2.0.2", {"start": v(-37.5, 29) * mm, "mid": v(-36, 30.5) * mm, "end": v(-34.5, 29) * mm});
            skArc(sketch, "E48.2.0.3", {"start": v(-34.5, -31) * mm, "mid": v(-36, -32.5) * mm, "end": v(-37.5, -31) * mm});
            skLineSegment(sketch, "E48.3.0.0", {"start": v(-24.5, 29) * mm, "end": v(-24.5, -31) * mm});
            skLineSegment(sketch, "E48.3.0.1", {"start": v(-27.5, 29) * mm, "end": v(-27.5, -31) * mm});
            skArc(sketch, "E48.3.0.2", {"start": v(-27.5, 29) * mm, "mid": v(-26, 30.5) * mm, "end": v(-24.5, 29) * mm});
            skArc(sketch, "E48.3.0.3", {"start": v(-24.5, -31) * mm, "mid": v(-26, -32.5) * mm, "end": v(-27.5, -31) * mm});
            skLineSegment(sketch, "E48.4.0.0", {"start": v(-14.5, 29) * mm, "end": v(-14.5, -31) * mm});
            skLineSegment(sketch, "E48.4.0.1", {"start": v(-17.5, 29) * mm, "end": v(-17.5, -31) * mm});
            skArc(sketch, "E48.4.0.2", {"start": v(-17.5, 29) * mm, "mid": v(-16, 30.5) * mm, "end": v(-14.5, 29) * mm});
            skArc(sketch, "E48.4.0.3", {"start": v(-14.5, -31) * mm, "mid": v(-16, -32.5) * mm, "end": v(-17.5, -31) * mm});
            skLineSegment(sketch, "E48.5.0.0", {"start": v(-4.5, 29) * mm, "end": v(-4.5, -31) * mm});
            skLineSegment(sketch, "E48.5.0.1", {"start": v(-7.5, 29) * mm, "end": v(-7.5, -31) * mm});
            skArc(sketch, "E48.5.0.2", {"start": v(-7.5, 29) * mm, "mid": v(-6, 30.5) * mm, "end": v(-4.5, 29) * mm});
            skArc(sketch, "E48.5.0.3", {"start": v(-4.5, -31) * mm, "mid": v(-6, -32.5) * mm, "end": v(-7.5, -31) * mm});
            skLineSegment(sketch, "E48.6.0.0", {"start": v(5.5, 29) * mm, "end": v(5.5, -31) * mm});
            skLineSegment(sketch, "E48.6.0.1", {"start": v(2.5, 29) * mm, "end": v(2.5, -31) * mm});
            skArc(sketch, "E48.6.0.2", {"start": v(2.5, 29) * mm, "mid": v(4, 30.5) * mm, "end": v(5.5, 29) * mm});
            skArc(sketch, "E48.6.0.3", {"start": v(5.5, -31) * mm, "mid": v(4, -32.5) * mm, "end": v(2.5, -31) * mm});
            skLineSegment(sketch, "E48.7.0.0", {"start": v(15.5, 29) * mm, "end": v(15.5, -31) * mm});
            skLineSegment(sketch, "E48.7.0.1", {"start": v(12.5, 29) * mm, "end": v(12.5, -31) * mm});
            skArc(sketch, "E48.7.0.2", {"start": v(12.5, 29) * mm, "mid": v(14, 30.5) * mm, "end": v(15.5, 29) * mm});
            skArc(sketch, "E48.7.0.3", {"start": v(15.5, -31) * mm, "mid": v(14, -32.5) * mm, "end": v(12.5, -31) * mm});
            skLineSegment(sketch, "E48.8.0.0", {"start": v(25.5, 29) * mm, "end": v(25.5, -31) * mm});
            skLineSegment(sketch, "E48.8.0.1", {"start": v(22.5, 29) * mm, "end": v(22.5, -31) * mm});
            skArc(sketch, "E48.8.0.2", {"start": v(22.5, 29) * mm, "mid": v(24, 30.5) * mm, "end": v(25.5, 29) * mm});
            skArc(sketch, "E48.8.0.3", {"start": v(25.5, -31) * mm, "mid": v(24, -32.5) * mm, "end": v(22.5, -31) * mm});
            skLineSegment(sketch, "E48.9.0.0", {"start": v(35.5, 29) * mm, "end": v(35.5, -31) * mm});
            skLineSegment(sketch, "E48.9.0.1", {"start": v(32.5, 29) * mm, "end": v(32.5, -31) * mm});
            skArc(sketch, "E48.9.0.2", {"start": v(32.5, 29) * mm, "mid": v(34, 30.5) * mm, "end": v(35.5, 29) * mm});
            skArc(sketch, "E48.9.0.3", {"start": v(35.5, -31) * mm, "mid": v(34, -32.5) * mm, "end": v(32.5, -31) * mm});
            skLineSegment(sketch, "E48.direction1", {"start": v(-57.5, -31) * mm, "end": v(-47.5, -31) * mm, "construction": true});
            skSolve(sketch);
        }
        {
            var Q0;
            Q0=makeQuery(id+"F11.imprint","IMPRINT",FACE,{"disambiguationData":[TD([[makeQuery(id+"F11.imprint","IMPRINT",EDGE,{"derivedFrom":sQuery(id+"F11.wireOp",EDGE,"E47.0.startCap")}),-1.0]])]});
            var Q1;
            Q1=makeQuery(id+"F11.imprint","IMPRINT",FACE,{"disambiguationData":[TD([[makeQuery(id+"F11.imprint","IMPRINT",EDGE,{"derivedFrom":sQuery(id+"F11.wireOp",EDGE,"E48.1.0.0")}),-1.0]])]});
            var Q2;
            Q2=makeQuery(id+"F11.imprint","IMPRINT",FACE,{"disambiguationData":[TD([[makeQuery(id+"F11.imprint","IMPRINT",EDGE,{"derivedFrom":sQuery(id+"F11.wireOp",EDGE,"E48.2.0.0")}),-1.0]])]});
            var Q3;
            Q3=makeQuery(id+"F11.imprint","IMPRINT",FACE,{"disambiguationData":[TD([[makeQuery(id+"F11.imprint","IMPRINT",EDGE,{"derivedFrom":sQuery(id+"F11.wireOp",EDGE,"E48.3.0.0")}),-1.0]])]});
            var Q4;
            Q4=makeQuery(id+"F11.imprint","IMPRINT",FACE,{"disambiguationData":[TD([[makeQuery(id+"F11.imprint","IMPRINT",EDGE,{"derivedFrom":sQuery(id+"F11.wireOp",EDGE,"E48.4.0.0")}),-1.0]])]});
            var Q5;
            Q5=makeQuery(id+"F11.imprint","IMPRINT",FACE,{"disambiguationData":[TD([[makeQuery(id+"F11.imprint","IMPRINT",EDGE,{"derivedFrom":sQuery(id+"F11.wireOp",EDGE,"E48.5.0.0")}),-1.0]])]});
            var Q6;
            Q6=makeQuery(id+"F11.imprint","IMPRINT",FACE,{"disambiguationData":[TD([[makeQuery(id+"F11.imprint","IMPRINT",EDGE,{"derivedFrom":sQuery(id+"F11.wireOp",EDGE,"E48.6.0.0")}),-1.0]])]});
            var Q7;
            Q7=makeQuery(id+"F11.imprint","IMPRINT",FACE,{"disambiguationData":[TD([[makeQuery(id+"F11.imprint","IMPRINT",EDGE,{"derivedFrom":sQuery(id+"F11.wireOp",EDGE,"E48.7.0.0")}),-1.0]])]});
            var Q8;
            Q8=makeQuery(id+"F11.imprint","IMPRINT",FACE,{"disambiguationData":[TD([[makeQuery(id+"F11.imprint","IMPRINT",EDGE,{"derivedFrom":sQuery(id+"F11.wireOp",EDGE,"E48.8.0.0")}),-1.0]])]});
            var Q9;
            Q9=makeQuery(id+"F11.imprint","IMPRINT",FACE,{"disambiguationData":[TD([[makeQuery(id+"F11.imprint","IMPRINT",EDGE,{"derivedFrom":sQuery(id+"F11.wireOp",EDGE,"E48.9.0.0")}),-1.0]])]});
            extrude(context, id + "F12", {"entities" : qUnion([Q0, Q1, Q2, Q3, Q4, Q5, Q6, Q7, Q8, Q9]), "operationType" : NewBodyOperationType.REMOVE, "endBound" : BoundingType.UP_TO_NEXT, "oppositeDirection" : true, "depth" : 25 * mm});
        }
    });
